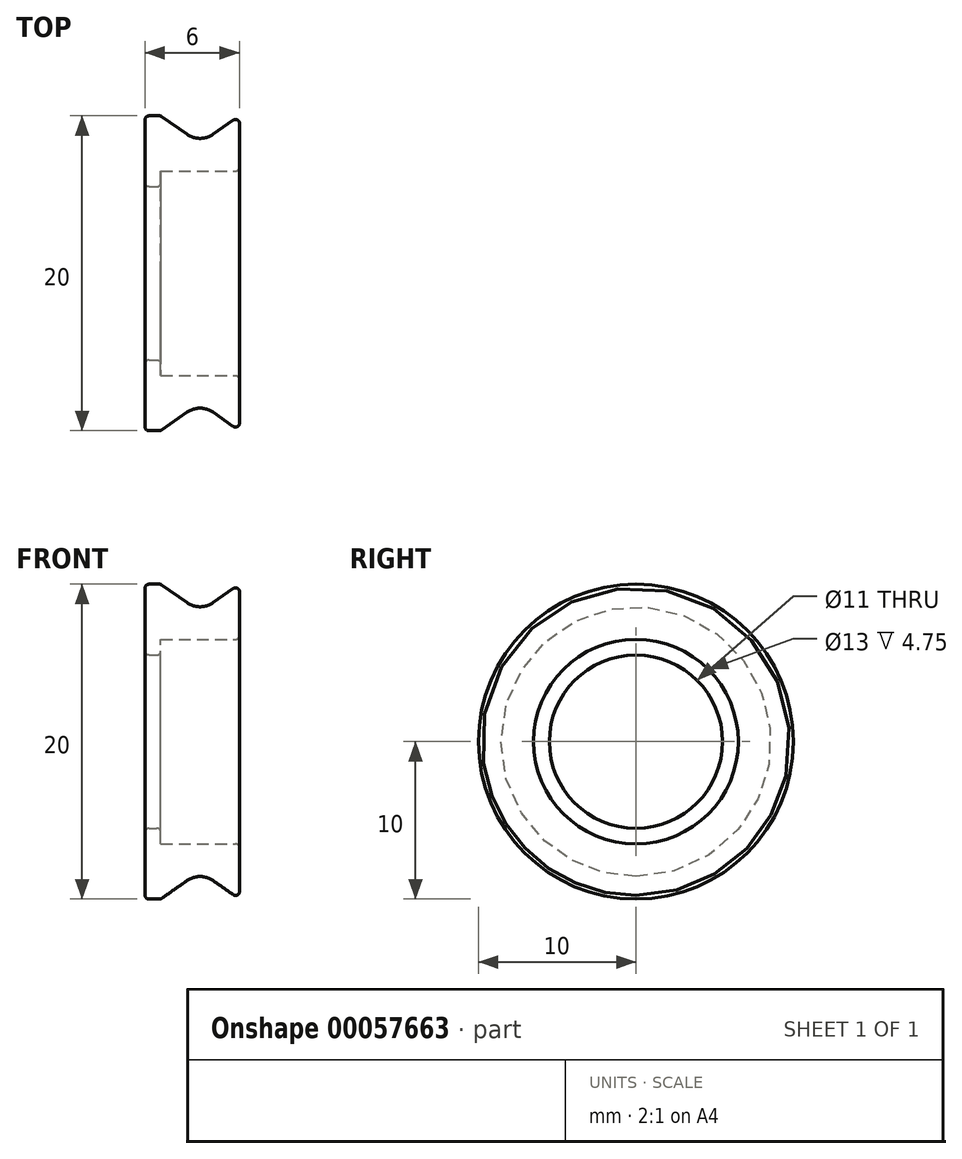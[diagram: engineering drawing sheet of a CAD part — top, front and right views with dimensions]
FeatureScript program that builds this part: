
annotation { "Feature Type Name" : "Feature", "Feature Type Description" : "" }
export const myFeature = defineFeature(function(context is Context, id is Id, definition is map)
    precondition{}
    {
        {
            var Q0;
            Q0=qCreatedBy(makeId("Front.planeOp"),FACE);
            var sketch = newSketch(context, id + "F0", { "sketchPlane" : qUnion([Q0])});
            skLineSegment(sketch, "E0", {"start": v(2.5, 0) * mm, "end": v(-2.5, 0) * mm, "construction": true});
            skLineSegment(sketch, "E1", {"start": v(-2.5, 6.5) * mm, "end": v(2.25, 6.5) * mm});
            skLineSegment(sketch, "E2", {"start": v(2.5, 6.75) * mm, "end": v(2.5, 9.52) * mm});
            skLineSegment(sketch, "E3", {"start": v(2.5, 10) * mm, "end": v(0, 8.25) * mm, "construction": true});
            skPoint(sketch, "E3.endSnap0", {"position": v(2.5, 8.25) * mm});
            skLineSegment(sketch, "E4", {"start": v(0, 8.25) * mm, "end": v(-2.5, 10) * mm, "construction": true});
            skLineSegment(sketch, "E5", {"start": v(0, 8.25) * mm, "end": v(0, 0) * mm, "construction": true});
            skPoint(sketch, "E6", {"position": v(0, 6.5) * mm});
            skCircle(sketch, "E7", {"center": v(0, 10) * mm, "radius": 1.43 * mm, "construction": true});
            skLineSegment(sketch, "E8", {"start": v(0, 10) * mm, "end": v(-2.5, 10) * mm, "construction": true});
            skLineSegment(sketch, "E9", {"start": v(0, 10) * mm, "end": v(0, 8.25) * mm, "construction": true});
            skLineSegment(sketch, "E10", {"start": v(0, 10) * mm, "end": v(2.5, 10) * mm, "construction": true});
            skLineSegment(sketch, "E11", {"start": v(-2.44, 9.95) * mm, "end": v(-0.82, 8.83) * mm});
            skLineSegment(sketch, "E12", {"start": v(2.1, 9.72) * mm, "end": v(0.82, 8.83) * mm});
            skArc(sketch, "E13", {"start": v(-0.82, 8.83) * mm, "mid": v(0, 8.57) * mm, "end": v(0.82, 8.83) * mm});
            skLineSegment(sketch, "E14", {"start": v(-2.5, 6.5) * mm, "end": v(-2.5, 5.75) * mm});
            skLineSegment(sketch, "E15", {"start": v(-2.75, 5.5) * mm, "end": v(-3.25, 5.5) * mm});
            skLineSegment(sketch, "E16", {"start": v(-3.5, 5.75) * mm, "end": v(-3.5, 9.75) * mm});
            skLineSegment(sketch, "E17", {"start": v(-3.25, 10) * mm, "end": v(-2.58, 10) * mm});
            skPoint(sketch, "E18.visualSharp", {"position": v(-3.5, 10) * mm});
            skArc(sketch, "E18.filletArc", {"start": v(-3.25, 10) * mm, "mid": v(-3.43, 9.93) * mm, "end": v(-3.5, 9.75) * mm});
            skPoint(sketch, "E19.visualSharp", {"position": v(-3.5, 5.5) * mm});
            skArc(sketch, "E19.filletArc", {"start": v(-3.5, 5.75) * mm, "mid": v(-3.43, 5.57) * mm, "end": v(-3.25, 5.5) * mm});
            skPoint(sketch, "E20.visualSharp", {"position": v(2.5, 6.5) * mm});
            skArc(sketch, "E20.filletArc", {"start": v(2.25, 6.5) * mm, "mid": v(2.43, 6.57) * mm, "end": v(2.5, 6.75) * mm});
            skPoint(sketch, "E21.visualSharp", {"position": v(-2.5, 5.5) * mm});
            skArc(sketch, "E21.filletArc", {"start": v(-2.75, 5.5) * mm, "mid": v(-2.57, 5.57) * mm, "end": v(-2.5, 5.75) * mm});
            skPoint(sketch, "E22.visualSharp", {"position": v(-2.5, 10) * mm});
            skArc(sketch, "E22.filletArc", {"start": v(-2.44, 9.95) * mm, "mid": v(-2.5, 9.99) * mm, "end": v(-2.58, 10) * mm});
            skPoint(sketch, "E23.visualSharp", {"position": v(2.5, 10) * mm});
            skArc(sketch, "E23.filletArc", {"start": v(2.5, 9.52) * mm, "mid": v(2.37, 9.74) * mm, "end": v(2.1, 9.72) * mm});
            skSolve(sketch);
        }
        {
            var Q0;
            Q0=makeQuery(id+"F0.imprint","IMPRINT",FACE,{"disambiguationData":[TD([[makeQuery(id+"F0.imprint","IMPRINT",EDGE,{"derivedFrom":sQuery(id+"F0.wireOp",EDGE,"E1")}),1.0]])]});
            var Q1;
            Q1=sQuery(id+"F0.wireOp",EDGE,"E0");
            revolve(context, id + "F1", {"entities" : qUnion([Q0]), "axis" : qUnion([Q1]), "revolveType" : RevolveType.FULL});
        }
    });
